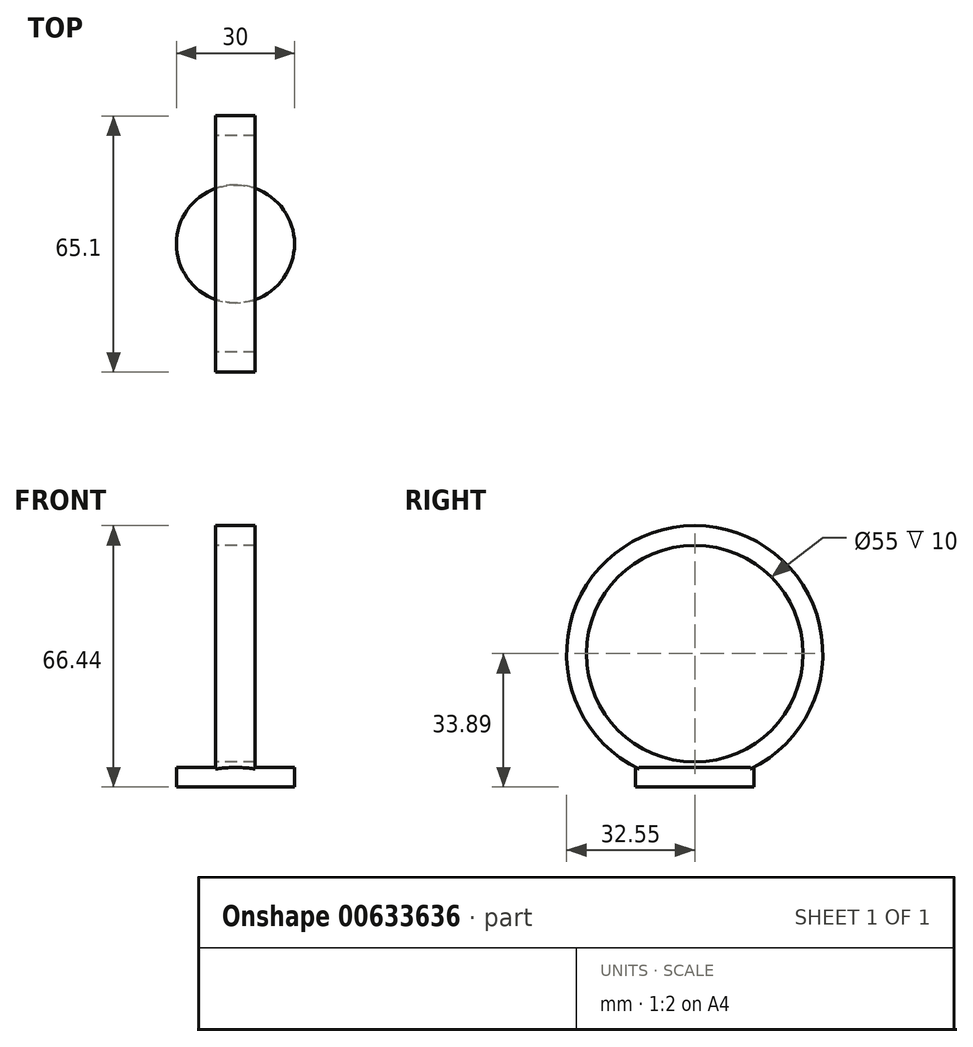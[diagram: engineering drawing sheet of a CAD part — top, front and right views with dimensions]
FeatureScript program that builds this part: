
annotation { "Feature Type Name" : "Feature", "Feature Type Description" : "" }
export const myFeature = defineFeature(function(context is Context, id is Id, definition is map)
    precondition{}
    {
        {
            var Q0;
            Q0=qCreatedBy(makeId("Top.planeOp"),FACE);
            var sketch = newSketch(context, id + "F0", { "sketchPlane" : qUnion([Q0])});
            skCircle(sketch, "E0", {"center": v(0, 0) * mm, "radius": 15 * mm});
            skSolve(sketch);
        }
        {
            var Q0;
            Q0=qCreatedBy(makeId("Right.planeOp"),FACE);
            var sketch = newSketch(context, id + "F1", { "sketchPlane" : qUnion([Q0])});
            skLineSegment(sketch, "E1", {"start": v(0, 0) * mm, "end": v(-15, 0) * mm, "construction": true});
            skLineSegment(sketch, "E2", {"start": v(0, 0) * mm, "end": v(15, 0) * mm, "construction": true});
            skLineSegment(sketch, "E3", {"start": v(0, 0) * mm, "end": v(-32.5, 0) * mm, "construction": true});
            skLineSegment(sketch, "E4", {"start": v(-32.5, 0) * mm, "end": v(-32.5, 43.19) * mm, "construction": true});
            skCircle(sketch, "E5", {"center": v(0, 28.9) * mm, "radius": 32.55 * mm});
            skPoint(sketch, "E5.third.point", {"position": v(-32.5, 27.05) * mm});
            skCircle(sketch, "E6", {"center": v(0, 28.9) * mm, "radius": 27.5 * mm});
            skSolve(sketch);
        }
        {
            var Q0;
            Q0 = qSketchRegion(id + "F0", true);
            extrude(context, id + "F2", {"entities" : qUnion([Q0]), "oppositeDirection" : true, "depth" : 5 * mm, "offsetDistance" : 25 * mm});
        }
        {
            var Q0;
            Q0=makeQuery(id+"F1.imprint","IMPRINT",FACE,{"disambiguationData":[TD([[makeQuery(id+"F1.imprint","IMPRINT",EDGE,{"derivedFrom":sQuery(id+"F1.wireOp",EDGE,"E5")}),1.0]])]});
            extrude(context, id + "F3", {"entities" : qUnion([Q0]), "operationType" : NewBodyOperationType.ADD, "endBound" : BoundingType.SYMMETRIC, "depth" : 10 * mm, "offsetDistance" : 25 * mm});
        }
    });
